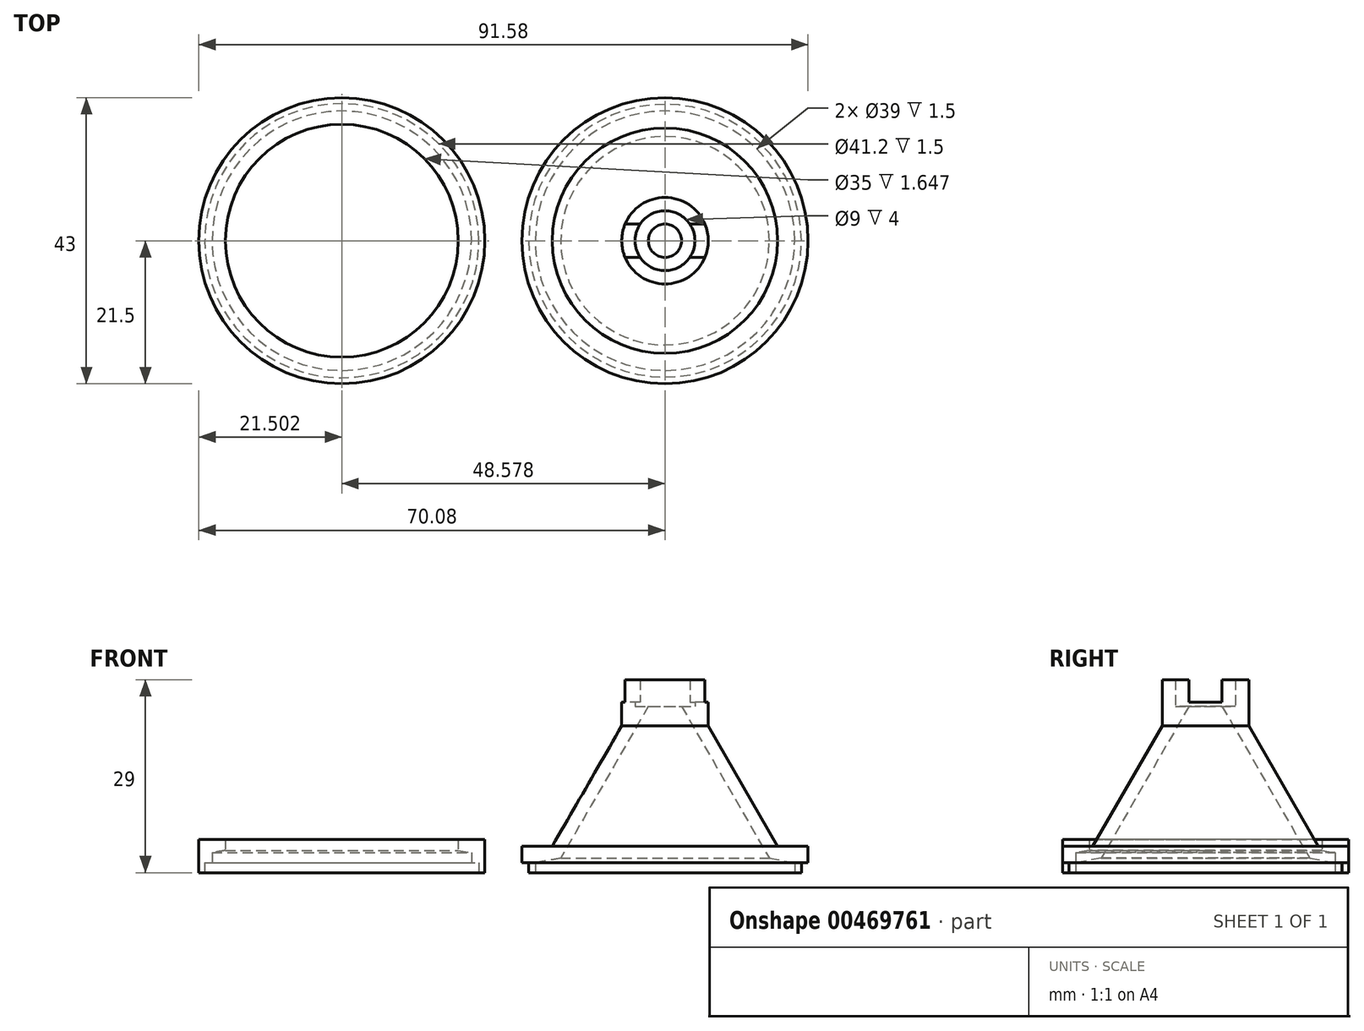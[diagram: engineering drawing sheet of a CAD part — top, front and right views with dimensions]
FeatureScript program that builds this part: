
annotation { "Feature Type Name" : "Feature", "Feature Type Description" : "" }
export const myFeature = defineFeature(function(context is Context, id is Id, definition is map)
    precondition{}
    {
        {
            var Q0;
            Q0=qCreatedBy(makeId("Front.planeOp"),FACE);
            var sketch = newSketch(context, id + "F0", { "sketchPlane" : qUnion([Q0])});
            skLineSegment(sketch, "E0", {"start": v(-19.5, 0) * mm, "end": v(-20.5, 0) * mm});
            skLineSegment(sketch, "E1", {"start": v(-21.5, 1.5) * mm, "end": v(-21.5, 4) * mm});
            skLineSegment(sketch, "E2", {"start": v(-21.5, 4) * mm, "end": v(-16.93, 4) * mm});
            skLineSegment(sketch, "E3", {"start": v(-16.93, 4) * mm, "end": v(-6.5, 22.07) * mm});
            skLineSegment(sketch, "E4", {"start": v(-6.5, 22.07) * mm, "end": v(-6.5, 29) * mm});
            skLineSegment(sketch, "E5", {"start": v(-6.5, 29) * mm, "end": v(-4.5, 29) * mm});
            skLineSegment(sketch, "E6", {"start": v(-4.5, 29) * mm, "end": v(-4.5, 25) * mm});
            skLineSegment(sketch, "E7", {"start": v(-4.5, 25) * mm, "end": v(-2.5, 25) * mm});
            skLineSegment(sketch, "E8", {"start": v(-2.5, 25) * mm, "end": v(-15.68, 2.17) * mm});
            skLineSegment(sketch, "E9", {"start": v(-15.68, 2.17) * mm, "end": v(-19.5, 1.5) * mm});
            skLineSegment(sketch, "E10", {"start": v(-19.5, 1.5) * mm, "end": v(-19.5, 0) * mm});
            skLineSegment(sketch, "E11", {"start": v(0, 0) * mm, "end": v(0, 30.95) * mm, "construction": true});
            skLineSegment(sketch, "E12", {"start": v(-21.5, 1.5) * mm, "end": v(-20.5, 1.5) * mm});
            skPoint(sketch, "E12.endSnap0", {"position": v(-20.5, 0) * mm});
            skLineSegment(sketch, "E13", {"start": v(-20.5, 1.5) * mm, "end": v(-20.5, 0) * mm});
            skSolve(sketch);
        }
        {
            var Q0;
            Q0=makeQuery(id+"F0.imprint","IMPRINT",FACE,{"disambiguationData":[TD([[makeQuery(id+"F0.imprint","IMPRINT",EDGE,{"derivedFrom":sQuery(id+"F0.wireOp",EDGE,"E0")}),-1.0]])]});
            var Q1;
            Q1=sQuery(id+"F0.wireOp",EDGE,"E11");
            revolve(context, id + "F1", {"entities" : qUnion([Q0]), "axis" : qUnion([Q1]), "revolveType" : RevolveType.FULL});
        }
        {
            var Q0;
            Q0=qCreatedBy(makeId("Right.planeOp"),FACE);
            var sketch = newSketch(context, id + "F2", { "sketchPlane" : qUnion([Q0])});
            skLineSegment(sketch, "E14.bottom", {"start": v(-2.5, 33.6) * mm, "end": v(2.5, 33.6) * mm});
            skLineSegment(sketch, "E14.top", {"start": v(-2.5, 25.6) * mm, "end": v(2.5, 25.6) * mm});
            skLineSegment(sketch, "E14.left", {"start": v(-2.5, 33.6) * mm, "end": v(-2.5, 25.6) * mm});
            skLineSegment(sketch, "E14.right", {"start": v(2.5, 33.6) * mm, "end": v(2.5, 25.6) * mm});
            skSolve(sketch);
        }
        {
            var Q0;
            Q0=makeQuery(id+"F2.imprint","IMPRINT",FACE,{"disambiguationData":[TD([[makeQuery(id+"F2.imprint","IMPRINT",EDGE,{"derivedFrom":sQuery(id+"F2.wireOp",EDGE,"E14.bottom")}),-1.0]])]});
            extrude(context, id + "F3", {"entities" : qUnion([Q0]), "operationType" : NewBodyOperationType.REMOVE, "endBound" : BoundingType.SYMMETRIC, "depth" : 15 * mm});
        }
        {
            var Q0;
            Q0=qCreatedBy(makeId("Front.planeOp"),FACE);
            var sketch = newSketch(context, id + "F4", { "sketchPlane" : qUnion([Q0])});
            skLineSegment(sketch, "E15", {"start": v(-70.08, 5) * mm, "end": v(-66.08, 5) * mm});
            skLineSegment(sketch, "E16", {"start": v(-66.08, 5) * mm, "end": v(-66.08, 3.35) * mm});
            skLineSegment(sketch, "E17", {"start": v(-66.08, 3.35) * mm, "end": v(-68.08, 3) * mm});
            skLineSegment(sketch, "E18", {"start": v(-68.08, 3) * mm, "end": v(-68.08, 1.5) * mm});
            skLineSegment(sketch, "E19", {"start": v(-48.58, -1.95) * mm, "end": v(-48.58, 12.75) * mm, "construction": true});
            skLineSegment(sketch, "E20", {"start": v(-68.08, 1.5) * mm, "end": v(-69.18, 1.5) * mm});
            skLineSegment(sketch, "E21", {"start": v(-69.18, 1.5) * mm, "end": v(-69.18, 0) * mm});
            skLineSegment(sketch, "E22", {"start": v(-69.18, 0) * mm, "end": v(-70.08, 0) * mm});
            skLineSegment(sketch, "E23", {"start": v(-70.08, 0) * mm, "end": v(-70.08, 5) * mm});
            skSolve(sketch);
        }
        {
            var Q0;
            Q0=makeQuery(id+"F4.imprint","IMPRINT",FACE,{"disambiguationData":[TD([[makeQuery(id+"F4.imprint","IMPRINT",EDGE,{"derivedFrom":sQuery(id+"F4.wireOp",EDGE,"E15")}),-1.0]])]});
            var Q1;
            Q1=sQuery(id+"F4.wireOp",EDGE,"E19");
            revolve(context, id + "F5", {"entities" : qUnion([Q0]), "axis" : qUnion([Q1]), "revolveType" : RevolveType.FULL});
        }
    });
